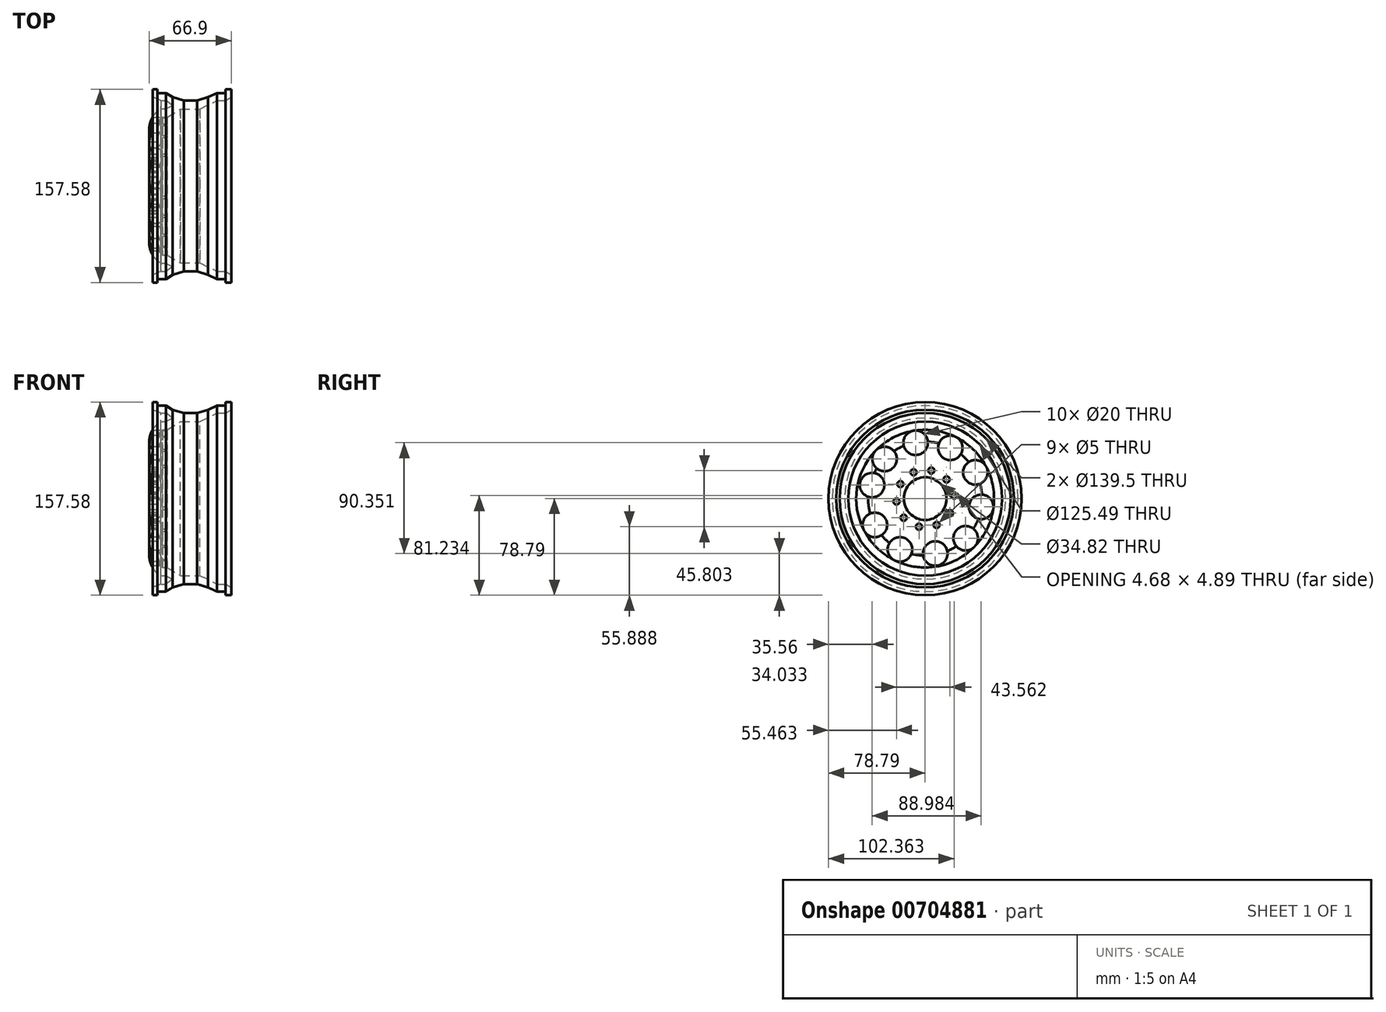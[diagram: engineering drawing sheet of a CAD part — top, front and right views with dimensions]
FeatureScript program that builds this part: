
annotation { "Feature Type Name" : "Feature", "Feature Type Description" : "" }
export const myFeature = defineFeature(function(context is Context, id is Id, definition is map)
    precondition{}
    {
        {
            var Q0;
            Q0=qCreatedBy(makeId("Front.planeOp"),FACE);
            var sketch = newSketch(context, id + "F0", { "sketchPlane" : qUnion([Q0])});
            skLineSegment(sketch, "E0", {"start": v(-25.54, 0) * mm, "end": v(-25.54, 46.25) * mm});
            skArc(sketch, "E1", {"start": v(-16.04, 62.97) * mm, "mid": v(-23, 55.86) * mm, "end": v(-25.54, 46.25) * mm});
            skLineSegment(sketch, "E2", {"start": v(-16.04, 62.97) * mm, "end": v(-12.2, 62.97) * mm});
            skLineSegment(sketch, "E3", {"start": v(-12.2, 62.97) * mm, "end": v(-6.55, 65.68) * mm});
            skLineSegment(sketch, "E4", {"start": v(-6.55, 65.68) * mm, "end": v(-11.98, 69.75) * mm});
            skLineSegment(sketch, "E5", {"start": v(-11.98, 69.75) * mm, "end": v(-16.04, 69.75) * mm});
            skLineSegment(sketch, "E6", {"start": v(-16.04, 69.75) * mm, "end": v(-22.82, 72.46) * mm});
            skLineSegment(sketch, "E7", {"start": v(-22.82, 72.46) * mm, "end": v(-22.82, 78.8) * mm});
            skLineSegment(sketch, "E8", {"start": v(-22.82, 78.8) * mm, "end": v(-18.76, 78.8) * mm});
            skLineSegment(sketch, "E9", {"start": v(-18.76, 78.8) * mm, "end": v(-18.76, 75.85) * mm});
            skLineSegment(sketch, "E10", {"start": v(-18.76, 75.85) * mm, "end": v(-11.98, 75.85) * mm});
            skLineSegment(sketch, "E11", {"start": v(-11.98, 75.85) * mm, "end": v(-6.55, 72.46) * mm});
            skLineSegment(sketch, "E12", {"start": v(-6.55, 72.46) * mm, "end": v(2.72, 69.75) * mm});
            skLineSegment(sketch, "E13", {"start": v(2.72, 69.75) * mm, "end": v(13.56, 69.75) * mm});
            skLineSegment(sketch, "E14", {"start": v(13.56, 69.75) * mm, "end": v(22.38, 72.46) * mm});
            skLineSegment(sketch, "E15", {"start": v(22.38, 72.46) * mm, "end": v(29.84, 75.85) * mm});
            skLineSegment(sketch, "E16", {"start": v(29.84, 75.85) * mm, "end": v(36.84, 75.85) * mm});
            skLineSegment(sketch, "E17", {"start": v(36.84, 75.85) * mm, "end": v(36.84, 78.8) * mm});
            skLineSegment(sketch, "E18", {"start": v(36.84, 78.8) * mm, "end": v(41.36, 78.8) * mm});
            skLineSegment(sketch, "E19", {"start": v(41.36, 78.8) * mm, "end": v(41.36, 72.46) * mm});
            skLineSegment(sketch, "E20", {"start": v(41.36, 72.46) * mm, "end": v(36.84, 69.75) * mm});
            skLineSegment(sketch, "E21", {"start": v(36.84, 69.75) * mm, "end": v(29.84, 69.75) * mm});
            skLineSegment(sketch, "E22", {"start": v(29.84, 69.75) * mm, "end": v(15.82, 62.75) * mm});
            skLineSegment(sketch, "E23", {"start": v(15.82, 62.75) * mm, "end": v(3.85, 62.75) * mm});
            skLineSegment(sketch, "E24", {"start": v(3.85, 62.75) * mm, "end": v(0, 62.75) * mm});
            skLineSegment(sketch, "E25", {"start": v(0, 62.75) * mm, "end": v(-11.07, 56.2) * mm});
            skLineSegment(sketch, "E26", {"start": v(-11.07, 56.2) * mm, "end": v(-14.69, 56.2) * mm});
            skArc(sketch, "E27", {"start": v(-14.69, 56.2) * mm, "mid": v(-18.04, 51.9) * mm, "end": v(-18.53, 46.47) * mm});
            skLineSegment(sketch, "E28", {"start": v(-18.53, 46.47) * mm, "end": v(-18.53, 0) * mm});
            skLineSegment(sketch, "E29", {"start": v(-18.53, 0) * mm, "end": v(-25.54, 0) * mm});
            skSolve(sketch);
        }
        {
            var Q0;
            Q0=makeQuery(id+"F0.imprint","IMPRINT",FACE,{"disambiguationData":[TD([[makeQuery(id+"F0.imprint","IMPRINT",EDGE,{"derivedFrom":sQuery(id+"F0.wireOp",EDGE,"E0")}),-1.0]])]});
            var Q1;
            Q1=sQuery(id+"F0.wireOp",EDGE,"E29");
            revolve(context, id + "F1", {"surfaceOperationType" : NewSurfaceOperationType.NEW, "entities" : qUnion([Q0]), "axis" : qUnion([Q1]), "revolveType" : RevolveType.FULL});
        }
        {
            var Q0;
            Q0=makeQuery(id+"F1.opRevolve","SWEPT_FACE",FACE,{"disambiguationData":[OSD([sQuery(id+"F0.wireOp",EDGE,"E0")])]});
            var sketch = newSketch(context, id + "F2", { "sketchPlane" : qUnion([Q0])});
            skCircle(sketch, "E30", {"center": v(0, 0) * mm, "radius": 17.41 * mm});
            skCircle(sketch, "E31", {"center": v(0, 0) * mm, "radius": 25.94 * mm});
            skCircle(sketch, "E32", {"center": v(-5, 22.9) * mm, "radius": 2.5 * mm});
            skCircle(sketch, "E33", {"center": v(9.41, 21.47) * mm, "radius": 2.5 * mm});
            skCircle(sketch, "E34", {"center": v(20.23, 11.84) * mm, "radius": 2.5 * mm});
            skCircle(sketch, "E35", {"center": v(23.33, -2.32) * mm, "radius": 2.5 * mm});
            skCircle(sketch, "E36", {"center": v(17.5, -15.59) * mm, "radius": 2.5 * mm});
            skCircle(sketch, "E37", {"center": v(5, -22.9) * mm, "radius": 2.5 * mm});
            skCircle(sketch, "E38", {"center": v(-9.41, -21.47) * mm, "radius": 2.5 * mm});
            skCircle(sketch, "E39", {"center": v(-20.23, -11.84) * mm, "radius": 2.5 * mm});
            skCircle(sketch, "E40", {"center": v(-23.72, 2.45) * mm, "radius": 2.5 * mm});
            skCircle(sketch, "E41", {"center": v(-17.5, 15.59) * mm, "radius": 2.5 * mm});
            skCircle(sketch, "E42", {"center": v(-20.54, 41.44) * mm, "radius": 10 * mm});
            skCircle(sketch, "E43", {"center": v(7.74, 45.6) * mm, "radius": 10 * mm});
            skCircle(sketch, "E44", {"center": v(33.06, 32.34) * mm, "radius": 10 * mm});
            skCircle(sketch, "E45", {"center": v(43.23, 11.04) * mm, "radius": 10 * mm});
            skCircle(sketch, "E46", {"center": v(40.97, -21.45) * mm, "radius": 10 * mm});
            skCircle(sketch, "E47", {"center": v(20.54, -41.44) * mm, "radius": 10 * mm});
            skCircle(sketch, "E48", {"center": v(-8.3, -44.76) * mm, "radius": 10 * mm});
            skCircle(sketch, "E49", {"center": v(-33.06, -32.34) * mm, "radius": 10 * mm});
            skCircle(sketch, "E50", {"center": v(-45.75, -6.73) * mm, "radius": 10 * mm});
            skCircle(sketch, "E51", {"center": v(-40.97, 21.45) * mm, "radius": 10 * mm});
            skSolve(sketch);
        }
        {
            var Q0;
            Q0=makeQuery(id+"F2.imprint","IMPRINT",FACE,{"disambiguationData":[TD([[makeQuery(id+"F2.imprint","IMPRINT",EDGE,{"derivedFrom":sQuery(id+"F2.wireOp",EDGE,"E30")}),1.0]])]});
            var Q1;
            Q1=sQuery(id+"F2.wireOp",EDGE,"E30");
            extrude(context, id + "F3", {"entities" : qUnion([Q0]), "operationType" : NewBodyOperationType.REMOVE, "surfaceEntities" : qUnion([Q1]), "oppositeDirection" : true, "depth" : 50 * mm, "offsetDistance" : 25 * mm});
        }
        {
            var Q0;
            {var subQ0=sQuery(id+"F2.wireOp",EDGE,"E42");var subQ1=makeQuery(id+"F1.opRevolve","SWEPT_EDGE",EDGE,{"disambiguationData":[OSD([sQuery(id+"F0.wireOp",EDGE,"E0"),sQuery(id+"F0.wireOp",EDGE,"E1")])]});var subQ2=makeQuery(id+"F2.imprint","INTERSECT",VERTEX,{"disambiguationData":[OD(0.0)],"derivedFrom":[subQ1,subQ0]});Q0=makeQuery(id+"F2.imprint","IMPRINT",FACE,{"disambiguationData":[TD([[makeQuery(id+"F2.imprint","IMPRINT",EDGE,{"disambiguationData":[TD([[subQ2,1.0]])],"derivedFrom":subQ0}),1.0]])]});}
            var Q1;
            {var subQ0=sQuery(id+"F2.wireOp",EDGE,"E42");var subQ1=makeQuery(id+"F1.opRevolve","SWEPT_EDGE",EDGE,{"disambiguationData":[OSD([sQuery(id+"F0.wireOp",EDGE,"E0"),sQuery(id+"F0.wireOp",EDGE,"E1")])]});var subQ2=makeQuery(id+"F2.imprint","INTERSECT",VERTEX,{"disambiguationData":[OD(0.0)],"derivedFrom":[subQ1,subQ0]});Q1=makeQuery(id+"F2.imprint","IMPRINT",FACE,{"disambiguationData":[TD([[makeQuery(id+"F2.imprint","IMPRINT",EDGE,{"disambiguationData":[TD([[subQ2,-1.0]])],"derivedFrom":subQ0}),1.0]])]});}
            var Q2;
            {var subQ0=sQuery(id+"F2.wireOp",EDGE,"E43");var subQ1=makeQuery(id+"F1.opRevolve","SWEPT_EDGE",EDGE,{"disambiguationData":[OSD([sQuery(id+"F0.wireOp",EDGE,"E0"),sQuery(id+"F0.wireOp",EDGE,"E1")])]});var subQ2=makeQuery(id+"F2.imprint","INTERSECT",VERTEX,{"disambiguationData":[OD(0.0)],"derivedFrom":[subQ1,subQ0]});Q2=makeQuery(id+"F2.imprint","IMPRINT",FACE,{"disambiguationData":[TD([[makeQuery(id+"F2.imprint","IMPRINT",EDGE,{"disambiguationData":[TD([[subQ2,1.0]])],"derivedFrom":subQ0}),1.0]])]});}
            var Q3;
            {var subQ0=sQuery(id+"F2.wireOp",EDGE,"E43");var subQ1=makeQuery(id+"F1.opRevolve","SWEPT_EDGE",EDGE,{"disambiguationData":[OSD([sQuery(id+"F0.wireOp",EDGE,"E0"),sQuery(id+"F0.wireOp",EDGE,"E1")])]});var subQ2=makeQuery(id+"F2.imprint","INTERSECT",VERTEX,{"disambiguationData":[OD(0.0)],"derivedFrom":[subQ1,subQ0]});Q3=makeQuery(id+"F2.imprint","IMPRINT",FACE,{"disambiguationData":[TD([[makeQuery(id+"F2.imprint","IMPRINT",EDGE,{"disambiguationData":[TD([[subQ2,-1.0]])],"derivedFrom":subQ0}),1.0]])]});}
            var Q4;
            {var subQ0=sQuery(id+"F2.wireOp",EDGE,"E44");var subQ1=makeQuery(id+"F1.opRevolve","SWEPT_EDGE",EDGE,{"disambiguationData":[OSD([sQuery(id+"F0.wireOp",EDGE,"E0"),sQuery(id+"F0.wireOp",EDGE,"E1")])]});var subQ2=makeQuery(id+"F2.imprint","INTERSECT",VERTEX,{"disambiguationData":[OD(0.0)],"derivedFrom":[subQ1,subQ0]});Q4=makeQuery(id+"F2.imprint","IMPRINT",FACE,{"disambiguationData":[TD([[makeQuery(id+"F2.imprint","IMPRINT",EDGE,{"disambiguationData":[TD([[subQ2,1.0]])],"derivedFrom":subQ0}),1.0]])]});}
            var Q5;
            {var subQ0=sQuery(id+"F2.wireOp",EDGE,"E44");var subQ1=makeQuery(id+"F1.opRevolve","SWEPT_EDGE",EDGE,{"disambiguationData":[OSD([sQuery(id+"F0.wireOp",EDGE,"E0"),sQuery(id+"F0.wireOp",EDGE,"E1")])]});var subQ2=makeQuery(id+"F2.imprint","INTERSECT",VERTEX,{"disambiguationData":[OD(0.0)],"derivedFrom":[subQ1,subQ0]});Q5=makeQuery(id+"F2.imprint","IMPRINT",FACE,{"disambiguationData":[TD([[makeQuery(id+"F2.imprint","IMPRINT",EDGE,{"disambiguationData":[TD([[subQ2,-1.0]])],"derivedFrom":subQ0}),1.0]])]});}
            var Q6;
            {var subQ0=sQuery(id+"F2.wireOp",EDGE,"E45");var subQ1=makeQuery(id+"F1.opRevolve","SWEPT_EDGE",EDGE,{"disambiguationData":[OSD([sQuery(id+"F0.wireOp",EDGE,"E0"),sQuery(id+"F0.wireOp",EDGE,"E1")])]});var subQ2=makeQuery(id+"F2.imprint","INTERSECT",VERTEX,{"disambiguationData":[OD(0.0)],"derivedFrom":[subQ1,subQ0]});Q6=makeQuery(id+"F2.imprint","IMPRINT",FACE,{"disambiguationData":[TD([[makeQuery(id+"F2.imprint","IMPRINT",EDGE,{"disambiguationData":[TD([[subQ2,1.0]])],"derivedFrom":subQ0}),1.0]])]});}
            var Q7;
            {var subQ0=sQuery(id+"F2.wireOp",EDGE,"E45");var subQ1=makeQuery(id+"F1.opRevolve","SWEPT_EDGE",EDGE,{"disambiguationData":[OSD([sQuery(id+"F0.wireOp",EDGE,"E0"),sQuery(id+"F0.wireOp",EDGE,"E1")])]});var subQ2=makeQuery(id+"F2.imprint","INTERSECT",VERTEX,{"disambiguationData":[OD(0.0)],"derivedFrom":[subQ1,subQ0]});Q7=makeQuery(id+"F2.imprint","IMPRINT",FACE,{"disambiguationData":[TD([[makeQuery(id+"F2.imprint","IMPRINT",EDGE,{"disambiguationData":[TD([[subQ2,-1.0]])],"derivedFrom":subQ0}),1.0]])]});}
            var Q8;
            {var subQ0=sQuery(id+"F2.wireOp",EDGE,"18d839aa-102b-44fb-bd46-29f6d2344a8f.4");var subQ3=sQuery(id+"F2.wireOp",EDGE,"E46");var subQ4=makeQuery(id+"F2.imprint","INTERSECT",VERTEX,{"derivedFrom":[subQ0,subQ3]});Q8=makeQuery(id+"F2.imprint","IMPRINT",FACE,{"disambiguationData":[TD([[makeQuery(id+"F2.imprint","IMPRINT",EDGE,{"disambiguationData":[TD([[subQ4,1.0]])],"derivedFrom":subQ0}),-1.0]])]});}
            var Q9;
            {var subQ0=sQuery(id+"F2.wireOp",EDGE,"E46");var subQ1=makeQuery(id+"F1.opRevolve","SWEPT_EDGE",EDGE,{"disambiguationData":[OSD([sQuery(id+"F0.wireOp",EDGE,"E0"),sQuery(id+"F0.wireOp",EDGE,"E1")])]});var subQ2=makeQuery(id+"F2.imprint","INTERSECT",VERTEX,{"disambiguationData":[OD(0.0)],"derivedFrom":[subQ1,subQ0]});Q9=makeQuery(id+"F2.imprint","IMPRINT",FACE,{"disambiguationData":[TD([[makeQuery(id+"F2.imprint","IMPRINT",EDGE,{"disambiguationData":[TD([[subQ2,1.0]])],"derivedFrom":subQ0}),1.0]])]});}
            var Q10;
            {var subQ0=sQuery(id+"F2.wireOp",EDGE,"E46");var subQ1=makeQuery(id+"F1.opRevolve","SWEPT_EDGE",EDGE,{"disambiguationData":[OSD([sQuery(id+"F0.wireOp",EDGE,"E0"),sQuery(id+"F0.wireOp",EDGE,"E1")])]});var subQ2=makeQuery(id+"F2.imprint","INTERSECT",VERTEX,{"disambiguationData":[OD(0.0)],"derivedFrom":[subQ1,subQ0]});Q10=makeQuery(id+"F2.imprint","IMPRINT",FACE,{"disambiguationData":[TD([[makeQuery(id+"F2.imprint","IMPRINT",EDGE,{"disambiguationData":[TD([[subQ2,-1.0]])],"derivedFrom":subQ0}),1.0]])]});}
            var Q11;
            {var subQ0=sQuery(id+"F2.wireOp",EDGE,"E47");var subQ1=makeQuery(id+"F1.opRevolve","SWEPT_EDGE",EDGE,{"disambiguationData":[OSD([sQuery(id+"F0.wireOp",EDGE,"E0"),sQuery(id+"F0.wireOp",EDGE,"E1")])]});var subQ2=makeQuery(id+"F2.imprint","INTERSECT",VERTEX,{"disambiguationData":[OD(0.0)],"derivedFrom":[subQ1,subQ0]});Q11=makeQuery(id+"F2.imprint","IMPRINT",FACE,{"disambiguationData":[TD([[makeQuery(id+"F2.imprint","IMPRINT",EDGE,{"disambiguationData":[TD([[subQ2,-1.0]])],"derivedFrom":subQ0}),1.0]])]});}
            var Q12;
            {var subQ0=sQuery(id+"F2.wireOp",EDGE,"E47");var subQ1=makeQuery(id+"F1.opRevolve","SWEPT_EDGE",EDGE,{"disambiguationData":[OSD([sQuery(id+"F0.wireOp",EDGE,"E0"),sQuery(id+"F0.wireOp",EDGE,"E1")])]});var subQ2=makeQuery(id+"F2.imprint","INTERSECT",VERTEX,{"disambiguationData":[OD(0.0)],"derivedFrom":[subQ1,subQ0]});Q12=makeQuery(id+"F2.imprint","IMPRINT",FACE,{"disambiguationData":[TD([[makeQuery(id+"F2.imprint","IMPRINT",EDGE,{"disambiguationData":[TD([[subQ2,1.0]])],"derivedFrom":subQ0}),1.0]])]});}
            var Q13;
            {var subQ0=sQuery(id+"F2.wireOp",EDGE,"E48");var subQ1=makeQuery(id+"F1.opRevolve","SWEPT_EDGE",EDGE,{"disambiguationData":[OSD([sQuery(id+"F0.wireOp",EDGE,"E0"),sQuery(id+"F0.wireOp",EDGE,"E1")])]});var subQ2=makeQuery(id+"F2.imprint","INTERSECT",VERTEX,{"disambiguationData":[OD(0.0)],"derivedFrom":[subQ1,subQ0]});Q13=makeQuery(id+"F2.imprint","IMPRINT",FACE,{"disambiguationData":[TD([[makeQuery(id+"F2.imprint","IMPRINT",EDGE,{"disambiguationData":[TD([[subQ2,-1.0]])],"derivedFrom":subQ0}),1.0]])]});}
            var Q14;
            {var subQ0=sQuery(id+"F2.wireOp",EDGE,"E48");var subQ1=makeQuery(id+"F1.opRevolve","SWEPT_EDGE",EDGE,{"disambiguationData":[OSD([sQuery(id+"F0.wireOp",EDGE,"E0"),sQuery(id+"F0.wireOp",EDGE,"E1")])]});var subQ2=makeQuery(id+"F2.imprint","INTERSECT",VERTEX,{"disambiguationData":[OD(0.0)],"derivedFrom":[subQ1,subQ0]});Q14=makeQuery(id+"F2.imprint","IMPRINT",FACE,{"disambiguationData":[TD([[makeQuery(id+"F2.imprint","IMPRINT",EDGE,{"disambiguationData":[TD([[subQ2,1.0]])],"derivedFrom":subQ0}),1.0]])]});}
            var Q15;
            {var subQ0=sQuery(id+"F2.wireOp",EDGE,"E49");var subQ1=makeQuery(id+"F1.opRevolve","SWEPT_EDGE",EDGE,{"disambiguationData":[OSD([sQuery(id+"F0.wireOp",EDGE,"E0"),sQuery(id+"F0.wireOp",EDGE,"E1")])]});var subQ2=makeQuery(id+"F2.imprint","INTERSECT",VERTEX,{"disambiguationData":[OD(0.0)],"derivedFrom":[subQ1,subQ0]});Q15=makeQuery(id+"F2.imprint","IMPRINT",FACE,{"disambiguationData":[TD([[makeQuery(id+"F2.imprint","IMPRINT",EDGE,{"disambiguationData":[TD([[subQ2,-1.0]])],"derivedFrom":subQ0}),1.0]])]});}
            var Q16;
            {var subQ0=sQuery(id+"F2.wireOp",EDGE,"E49");var subQ1=makeQuery(id+"F1.opRevolve","SWEPT_EDGE",EDGE,{"disambiguationData":[OSD([sQuery(id+"F0.wireOp",EDGE,"E0"),sQuery(id+"F0.wireOp",EDGE,"E1")])]});var subQ2=makeQuery(id+"F2.imprint","INTERSECT",VERTEX,{"disambiguationData":[OD(0.0)],"derivedFrom":[subQ1,subQ0]});Q16=makeQuery(id+"F2.imprint","IMPRINT",FACE,{"disambiguationData":[TD([[makeQuery(id+"F2.imprint","IMPRINT",EDGE,{"disambiguationData":[TD([[subQ2,1.0]])],"derivedFrom":subQ0}),1.0]])]});}
            var Q17;
            {var subQ0=sQuery(id+"F2.wireOp",EDGE,"E50");var subQ1=makeQuery(id+"F1.opRevolve","SWEPT_EDGE",EDGE,{"disambiguationData":[OSD([sQuery(id+"F0.wireOp",EDGE,"E0"),sQuery(id+"F0.wireOp",EDGE,"E1")])]});var subQ2=makeQuery(id+"F2.imprint","INTERSECT",VERTEX,{"disambiguationData":[OD(0.0)],"derivedFrom":[subQ1,subQ0]});Q17=makeQuery(id+"F2.imprint","IMPRINT",FACE,{"disambiguationData":[TD([[makeQuery(id+"F2.imprint","IMPRINT",EDGE,{"disambiguationData":[TD([[subQ2,-1.0]])],"derivedFrom":subQ0}),1.0]])]});}
            var Q18;
            {var subQ0=sQuery(id+"F2.wireOp",EDGE,"E50");var subQ1=makeQuery(id+"F1.opRevolve","SWEPT_EDGE",EDGE,{"disambiguationData":[OSD([sQuery(id+"F0.wireOp",EDGE,"E0"),sQuery(id+"F0.wireOp",EDGE,"E1")])]});var subQ2=makeQuery(id+"F2.imprint","INTERSECT",VERTEX,{"disambiguationData":[OD(0.0)],"derivedFrom":[subQ1,subQ0]});Q18=makeQuery(id+"F2.imprint","IMPRINT",FACE,{"disambiguationData":[TD([[makeQuery(id+"F2.imprint","IMPRINT",EDGE,{"disambiguationData":[TD([[subQ2,1.0]])],"derivedFrom":subQ0}),1.0]])]});}
            var Q19;
            {var subQ0=sQuery(id+"F2.wireOp",EDGE,"E51");var subQ1=makeQuery(id+"F1.opRevolve","SWEPT_EDGE",EDGE,{"disambiguationData":[OSD([sQuery(id+"F0.wireOp",EDGE,"E0"),sQuery(id+"F0.wireOp",EDGE,"E1")])]});var subQ2=makeQuery(id+"F2.imprint","INTERSECT",VERTEX,{"disambiguationData":[OD(0.0)],"derivedFrom":[subQ1,subQ0]});Q19=makeQuery(id+"F2.imprint","IMPRINT",FACE,{"disambiguationData":[TD([[makeQuery(id+"F2.imprint","IMPRINT",EDGE,{"disambiguationData":[TD([[subQ2,-1.0]])],"derivedFrom":subQ0}),1.0]])]});}
            var Q20;
            {var subQ0=sQuery(id+"F2.wireOp",EDGE,"E51");var subQ1=makeQuery(id+"F1.opRevolve","SWEPT_EDGE",EDGE,{"disambiguationData":[OSD([sQuery(id+"F0.wireOp",EDGE,"E0"),sQuery(id+"F0.wireOp",EDGE,"E1")])]});var subQ2=makeQuery(id+"F2.imprint","INTERSECT",VERTEX,{"disambiguationData":[OD(0.0)],"derivedFrom":[subQ1,subQ0]});Q20=makeQuery(id+"F2.imprint","IMPRINT",FACE,{"disambiguationData":[TD([[makeQuery(id+"F2.imprint","IMPRINT",EDGE,{"disambiguationData":[TD([[subQ2,1.0]])],"derivedFrom":subQ0}),1.0]])]});}
            var Q21;
            Q21=sQuery(id+"F2.wireOp",EDGE,"E42");
            var Q22;
            Q22=sQuery(id+"F2.wireOp",EDGE,"E43");
            var Q23;
            Q23=sQuery(id+"F2.wireOp",EDGE,"E44");
            var Q24;
            Q24=sQuery(id+"F2.wireOp",EDGE,"E45");
            var Q25;
            Q25=sQuery(id+"F2.wireOp",EDGE,"E46");
            var Q26;
            Q26=sQuery(id+"F2.wireOp",EDGE,"E47");
            var Q27;
            Q27=sQuery(id+"F2.wireOp",EDGE,"E48");
            var Q28;
            Q28=sQuery(id+"F2.wireOp",EDGE,"E49");
            var Q29;
            Q29=sQuery(id+"F2.wireOp",EDGE,"E50");
            var Q30;
            Q30=sQuery(id+"F2.wireOp",EDGE,"E51");
            extrude(context, id + "F4", {"entities" : qUnion([Q0, Q1, Q2, Q3, Q4, Q5, Q6, Q7, Q8, Q9, Q10, Q11, Q12, Q13, Q14, Q15, Q16, Q17, Q18, Q19, Q20]), "operationType" : NewBodyOperationType.REMOVE, "surfaceEntities" : qUnion([Q21, Q22, Q23, Q24, Q25, Q26, Q27, Q28, Q29, Q30]), "oppositeDirection" : true, "depth" : 30 * mm, "offsetDistance" : 25 * mm});
        }
        {
            var Q0;
            Q0=makeQuery(id+"F2.imprint","IMPRINT",FACE,{"disambiguationData":[TD([[makeQuery(id+"F2.imprint","IMPRINT",EDGE,{"derivedFrom":sQuery(id+"F2.wireOp",EDGE,"E32")}),1.0]])]});
            var Q1;
            Q1=makeQuery(id+"F2.imprint","IMPRINT",FACE,{"disambiguationData":[TD([[makeQuery(id+"F2.imprint","IMPRINT",EDGE,{"derivedFrom":sQuery(id+"F2.wireOp",EDGE,"E33")}),1.0]])]});
            var Q2;
            Q2=makeQuery(id+"F2.imprint","IMPRINT",FACE,{"disambiguationData":[TD([[makeQuery(id+"F2.imprint","IMPRINT",EDGE,{"derivedFrom":sQuery(id+"F2.wireOp",EDGE,"E34")}),1.0]])]});
            var Q3;
            Q3=makeQuery(id+"F2.imprint","IMPRINT",FACE,{"disambiguationData":[TD([[makeQuery(id+"F2.imprint","IMPRINT",EDGE,{"derivedFrom":sQuery(id+"F2.wireOp",EDGE,"E35")}),1.0]])]});
            var Q4;
            Q4=makeQuery(id+"F2.imprint","IMPRINT",FACE,{"disambiguationData":[TD([[makeQuery(id+"F2.imprint","IMPRINT",EDGE,{"derivedFrom":sQuery(id+"F2.wireOp",EDGE,"E36")}),1.0]])]});
            var Q5;
            Q5=makeQuery(id+"F2.imprint","IMPRINT",FACE,{"disambiguationData":[TD([[makeQuery(id+"F2.imprint","IMPRINT",EDGE,{"derivedFrom":sQuery(id+"F2.wireOp",EDGE,"E37")}),1.0]])]});
            var Q6;
            Q6=makeQuery(id+"F2.imprint","IMPRINT",FACE,{"disambiguationData":[TD([[makeQuery(id+"F2.imprint","IMPRINT",EDGE,{"derivedFrom":sQuery(id+"F2.wireOp",EDGE,"E39")}),1.0]])]});
            var Q7;
            {var subQ0=sQuery(id+"F2.wireOp",EDGE,"E40");var subQ1=sQuery(id+"F2.wireOp",EDGE,"E31");var subQ2=makeQuery(id+"F2.imprint","INTERSECT",VERTEX,{"disambiguationData":[OD(0.0)],"derivedFrom":[subQ1,subQ0]});Q7=makeQuery(id+"F2.imprint","IMPRINT",FACE,{"disambiguationData":[TD([[makeQuery(id+"F2.imprint","IMPRINT",EDGE,{"disambiguationData":[TD([[subQ2,-1.0]])],"derivedFrom":subQ1}),1.0]])]});}
            var Q8;
            Q8=makeQuery(id+"F2.imprint","IMPRINT",FACE,{"disambiguationData":[TD([[makeQuery(id+"F2.imprint","IMPRINT",EDGE,{"derivedFrom":sQuery(id+"F2.wireOp",EDGE,"E41")}),1.0]])]});
            var Q9;
            Q9=makeQuery(id+"F2.imprint","IMPRINT",FACE,{"disambiguationData":[TD([[makeQuery(id+"F2.imprint","IMPRINT",EDGE,{"derivedFrom":sQuery(id+"F2.wireOp",EDGE,"E38")}),1.0]])]});
            var Q10;
            Q10=sQuery(id+"F2.wireOp",EDGE,"E33");
            var Q11;
            Q11=sQuery(id+"F2.wireOp",EDGE,"E32");
            var Q12;
            Q12=sQuery(id+"F2.wireOp",EDGE,"E41");
            var Q13;
            Q13=sQuery(id+"F2.wireOp",EDGE,"E40");
            var Q14;
            Q14=sQuery(id+"F2.wireOp",EDGE,"E39");
            var Q15;
            Q15=sQuery(id+"F2.wireOp",EDGE,"E38");
            var Q16;
            Q16=sQuery(id+"F2.wireOp",EDGE,"E37");
            var Q17;
            Q17=sQuery(id+"F2.wireOp",EDGE,"E36");
            var Q18;
            Q18=sQuery(id+"F2.wireOp",EDGE,"E35");
            var Q19;
            Q19=sQuery(id+"F2.wireOp",EDGE,"E34");
            extrude(context, id + "F5", {"entities" : qUnion([Q0, Q1, Q2, Q3, Q4, Q5, Q6, Q7, Q8, Q9]), "operationType" : NewBodyOperationType.REMOVE, "surfaceEntities" : qUnion([Q10, Q11, Q12, Q13, Q14, Q15, Q16, Q17, Q18, Q19]), "oppositeDirection" : true, "depth" : 50 * mm, "offsetDistance" : 25 * mm});
        }
    });
